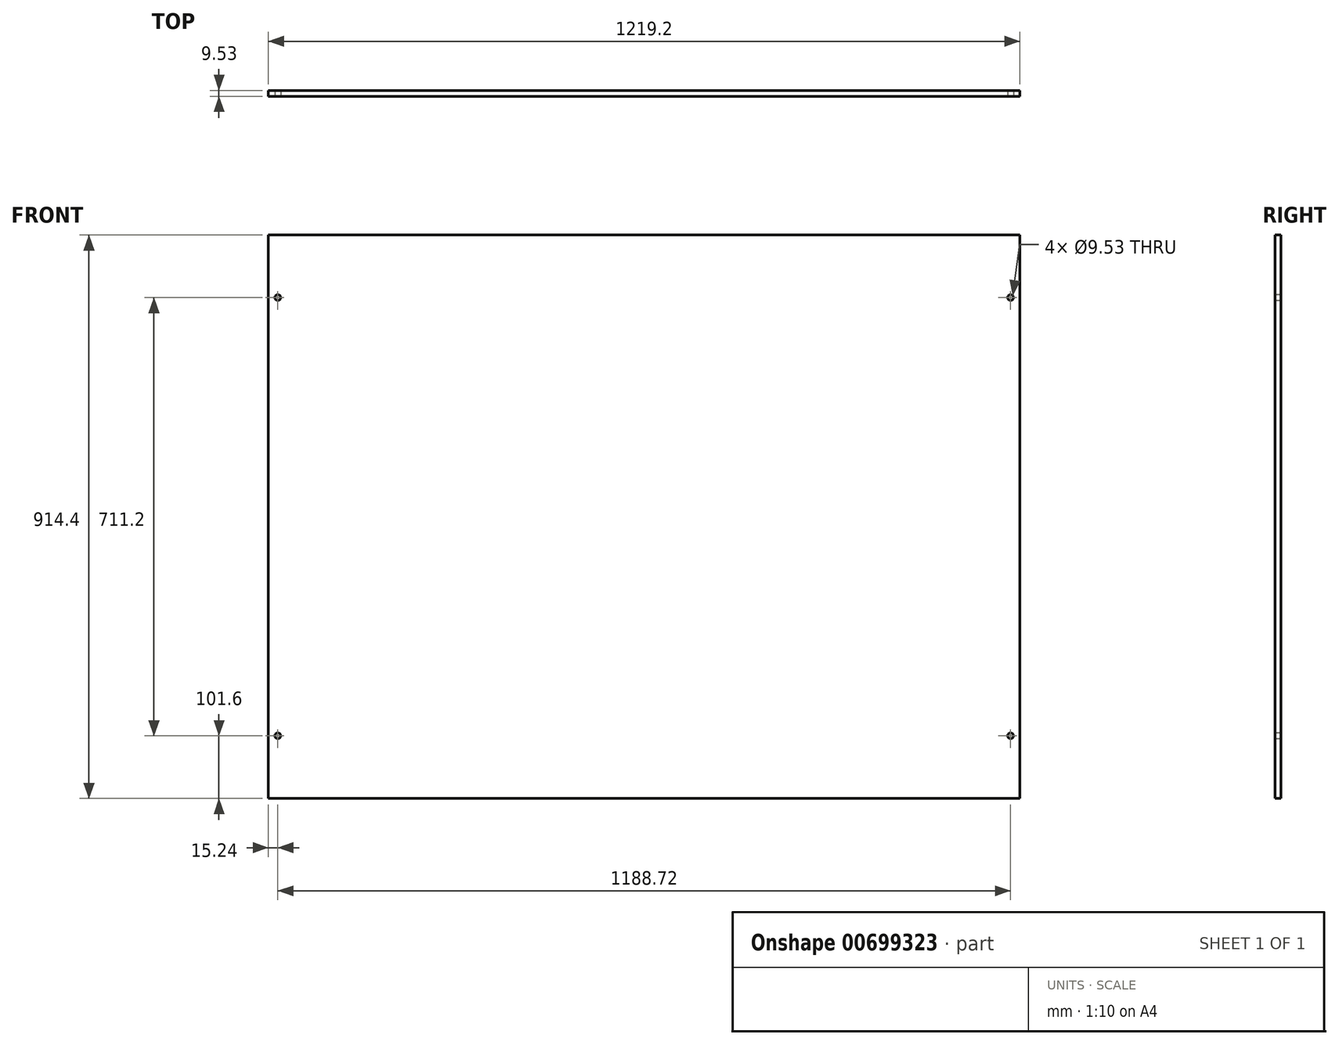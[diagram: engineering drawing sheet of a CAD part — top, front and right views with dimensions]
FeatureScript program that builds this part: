
annotation { "Feature Type Name" : "Feature", "Feature Type Description" : "" }
export const myFeature = defineFeature(function(context is Context, id is Id, definition is map)
    precondition{}
    {
        {
            var Q0;
            Q0=qCreatedBy(makeId("Front.planeOp"),FACE);
            var sketch = newSketch(context, id + "F0", { "sketchPlane" : qUnion([Q0])});
            skLineSegment(sketch, "E0.bottom", {"start": v(0, 0) * mm, "end": v(1219.2, 0) * mm});
            skLineSegment(sketch, "E0.top", {"start": v(0, 914.4) * mm, "end": v(1219.2, 914.4) * mm});
            skLineSegment(sketch, "E0.left", {"start": v(0, 0) * mm, "end": v(0, 914.4) * mm});
            skLineSegment(sketch, "E0.right", {"start": v(1219.2, 0) * mm, "end": v(1219.2, 914.4) * mm});
            skSolve(sketch);
        }
        {
            var Q0;
            Q0=makeQuery(id+"F0.imprint","IMPRINT",FACE,{"disambiguationData":[TD([[makeQuery(id+"F0.imprint","IMPRINT",EDGE,{"derivedFrom":sQuery(id+"F0.wireOp",EDGE,"E0.bottom")}),1.0]])]});
            extrude(context, id + "F1", {"entities" : qUnion([Q0]), "depth" : 9.52 * mm, "offsetDistance" : 25.4 * mm});
        }
        {
            var Q0;
            Q0=makeQuery(id+"F1.opExtrude","CAP_FACE",FACE,{"disambiguationData":[OSD([sQuery(id+"F0.wireOp",EDGE,"E0.bottom"),sQuery(id+"F0.wireOp",EDGE,"E0.top"),sQuery(id+"F0.wireOp",EDGE,"E0.left"),sQuery(id+"F0.wireOp",EDGE,"E0.right")])],"isStart":false});
            var sketch = newSketch(context, id + "F2", { "sketchPlane" : qUnion([Q0])});
            skCircle(sketch, "E1", {"center": v(1203.96, 812.8) * mm, "radius": 4.76 * mm});
            skCircle(sketch, "E2", {"center": v(1203.96, 101.6) * mm, "radius": 4.76 * mm});
            skCircle(sketch, "E3", {"center": v(15.24, 812.8) * mm, "radius": 4.76 * mm});
            skCircle(sketch, "E4", {"center": v(15.24, 101.6) * mm, "radius": 4.76 * mm});
            skSolve(sketch);
        }
        {
            var Q0;
            Q0=makeQuery(id+"F2.imprint","IMPRINT",FACE,{"disambiguationData":[TD([[makeQuery(id+"F2.imprint","IMPRINT",EDGE,{"derivedFrom":sQuery(id+"F2.wireOp",EDGE,"E3")}),1.0]])]});
            var Q1;
            Q1=makeQuery(id+"F2.imprint","IMPRINT",FACE,{"disambiguationData":[TD([[makeQuery(id+"F2.imprint","IMPRINT",EDGE,{"derivedFrom":sQuery(id+"F2.wireOp",EDGE,"E4")}),1.0]])]});
            var Q2;
            Q2=makeQuery(id+"F2.imprint","IMPRINT",FACE,{"disambiguationData":[TD([[makeQuery(id+"F2.imprint","IMPRINT",EDGE,{"derivedFrom":sQuery(id+"F2.wireOp",EDGE,"E2")}),1.0]])]});
            var Q3;
            Q3=makeQuery(id+"F2.imprint","IMPRINT",FACE,{"disambiguationData":[TD([[makeQuery(id+"F2.imprint","IMPRINT",EDGE,{"derivedFrom":sQuery(id+"F2.wireOp",EDGE,"E1")}),1.0]])]});
            extrude(context, id + "F3", {"entities" : qUnion([Q0, Q1, Q2, Q3]), "operationType" : NewBodyOperationType.REMOVE, "endBound" : BoundingType.THROUGH_ALL, "oppositeDirection" : true, "depth" : 25.4 * mm, "offsetDistance" : 25.4 * mm});
        }
    });
